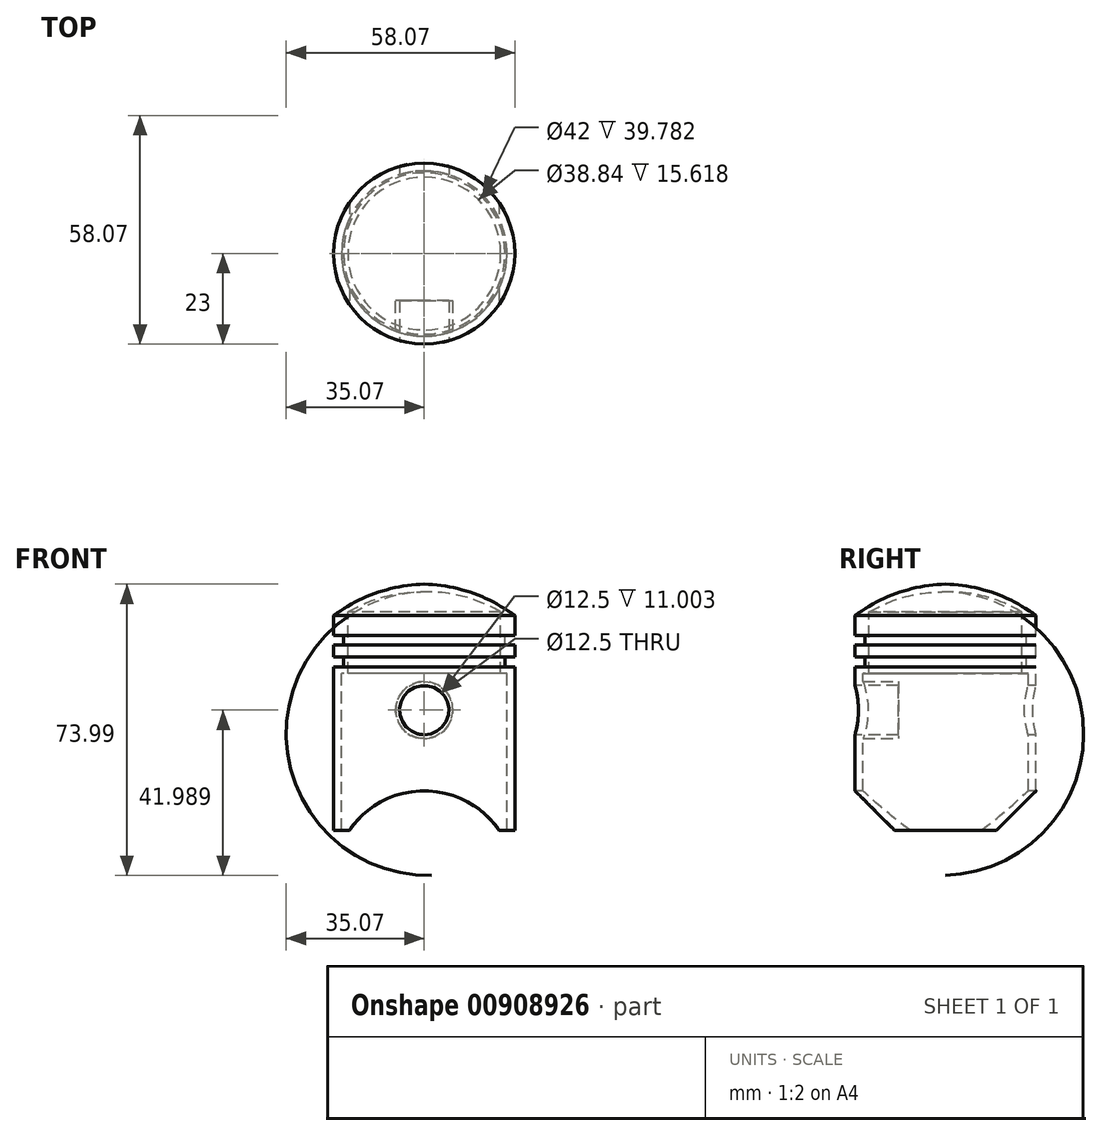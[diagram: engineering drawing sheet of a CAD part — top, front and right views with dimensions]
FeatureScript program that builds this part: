
annotation { "Feature Type Name" : "Feature", "Feature Type Description" : "" }
export const myFeature = defineFeature(function(context is Context, id is Id, definition is map)
    precondition{}
    {
        {
            var Q0;
            Q0=qCreatedBy(makeId("Front.planeOp"),FACE);
            var sketch = newSketch(context, id + "F0", { "sketchPlane" : qUnion([Q0])});
            skLineSegment(sketch, "E0", {"start": v(0, 62.5) * mm, "end": v(0, 60.5) * mm});
            skLineSegment(sketch, "E1", {"start": v(21, 0) * mm, "end": v(23, 0) * mm});
            skLineSegment(sketch, "E2", {"start": v(23, 0) * mm, "end": v(23, 41.5) * mm});
            skLineSegment(sketch, "E3", {"start": v(23, 41.5) * mm, "end": v(20.5, 41.5) * mm});
            skLineSegment(sketch, "E4", {"start": v(20.5, 41.5) * mm, "end": v(20.5, 44) * mm});
            skLineSegment(sketch, "E5", {"start": v(20.5, 44) * mm, "end": v(23, 44) * mm});
            skLineSegment(sketch, "E6", {"start": v(23, 44) * mm, "end": v(23, 47) * mm});
            skLineSegment(sketch, "E7", {"start": v(23, 47) * mm, "end": v(20.5, 47) * mm});
            skLineSegment(sketch, "E8", {"start": v(20.5, 47) * mm, "end": v(20.5, 49.5) * mm});
            skLineSegment(sketch, "E9", {"start": v(20.5, 49.5) * mm, "end": v(23, 49.5) * mm});
            skLineSegment(sketch, "E10", {"start": v(23, 49.5) * mm, "end": v(23, 54.5) * mm});
            skArc(sketch, "E11", {"start": v(23, 54.5) * mm, "mid": v(12.12, 60.3) * mm, "end": v(0, 62.5) * mm});
            skArc(sketch, "E12.0", {"start": v(19.42, 55.4) * mm, "mid": v(10.07, 59.33) * mm, "end": v(0, 60.5) * mm});
            skLineSegment(sketch, "E12.1", {"start": v(19.42, 39.88) * mm, "end": v(19.42, 55.4) * mm});
            skLineSegment(sketch, "E12.3", {"start": v(21, 0) * mm, "end": v(21, 39.78) * mm});
            skLineSegment(sketch, "E12.4", {"start": v(21, 39.78) * mm, "end": v(19.42, 39.78) * mm});
            skLineSegment(sketch, "E12.6", {"start": v(19.42, 39.78) * mm, "end": v(19.42, 39.88) * mm});
            skSolve(sketch);
        }
        {
            var Q0;
            Q0 = qSketchRegion(id + "F0", true);
            var Q1;
            Q1=sQuery(id+"F0.wireOp",EDGE,"E0");
            revolve(context, id + "F1", {"surfaceOperationType" : NewSurfaceOperationType.NEW, "entities" : qUnion([Q0]), "axis" : qUnion([Q1]), "revolveType" : RevolveType.FULL});
        }
        {
            var Q0;
            Q0=qCreatedBy(makeId("Front.planeOp"),FACE);
            var sketch = newSketch(context, id + "F2", { "sketchPlane" : qUnion([Q0])});
            skLineSegment(sketch, "E13", {"start": v(-19, 0) * mm, "end": v(19, 0) * mm});
            skLineSegment(sketch, "E14", {"start": v(0, 0) * mm, "end": v(0, 10) * mm, "construction": true});
            skArc(sketch, "E15", {"start": v(19, 0) * mm, "mid": v(0, 10) * mm, "end": v(-19, 0) * mm});
            skSolve(sketch);
        }
        {
            var Q0;
            Q0 = qSketchRegion(id + "F2", true);
            extrude(context, id + "F3", {"entities" : qUnion([Q0]), "operationType" : NewBodyOperationType.REMOVE, "endBound" : BoundingType.SYMMETRIC, "oppositeDirection" : true, "depth" : 65 * mm, "offsetDistance" : 25 * mm});
        }
        {
            var Q0;
            Q0=qCreatedBy(makeId("Front.planeOp"),FACE);
            var sketch = newSketch(context, id + "F4", { "sketchPlane" : qUnion([Q0])});
            skCircle(sketch, "E16", {"center": v(0, 30.5) * mm, "radius": 6.25 * mm});
            skLineSegment(sketch, "E17", {"start": v(0, 62.5) * mm, "end": v(0, 30.5) * mm, "construction": true});
            skSolve(sketch);
        }
        {
            var Q0;
            Q0 = qSketchRegion(id + "F4", true);
            extrude(context, id + "F5", {"entities" : qUnion([Q0]), "operationType" : NewBodyOperationType.REMOVE, "endBound" : BoundingType.SYMMETRIC, "oppositeDirection" : true, "depth" : 60 * mm, "offsetDistance" : 25 * mm});
        }
        {
            var Q0;
            Q0=qCreatedBy(makeId("Front.planeOp"),FACE);
            cPlane(context, id + "F6", {"entities" : qUnion([Q0]), "cplaneType" : CPlaneType.OFFSET, "offset" : 12 * mm, "width" : 150 * mm, "height" : 150 * mm});
        }
        {
            var Q0;
            Q0=qCreatedBy(id+"F6.planeOp",FACE);
            var sketch = newSketch(context, id + "F7", { "sketchPlane" : qUnion([Q0])});
            skCircle(sketch, "E18.0", {"center": v(0, 30.5) * mm, "radius": 6.25 * mm});
            skCircle(sketch, "E19", {"center": v(0, 30.5) * mm, "radius": 7.25 * mm});
            skSolve(sketch);
        }
        {
            var Q0;
            Q0 = qSketchRegion(id + "F7", true);
            extrude(context, id + "F8", {"entities" : qUnion([Q0]), "operationType" : NewBodyOperationType.ADD, "endBound" : BoundingType.UP_TO_NEXT, "depth" : 25 * mm, "offsetDistance" : 25 * mm});
        }
    });
